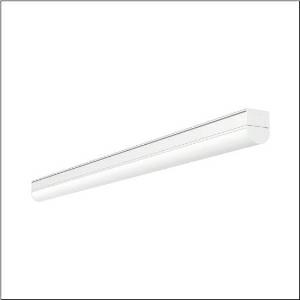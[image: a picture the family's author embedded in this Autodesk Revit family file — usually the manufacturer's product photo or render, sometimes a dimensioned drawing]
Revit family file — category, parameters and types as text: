
# Revit family: ecopack_31_51lj12mnm70a
name_source: partatom
category: Lighting Fixtures
units: mm (PartAtom-declared; Revit-internal decimal feet)

## family parameters
Cut with Voids When Loaded = No
Host = Face
Light Source = No
Part Type = Normal
Room Calculation Point = No
Round Connector Dimension = Use Diameter
Shared = No

## types (1)
- --- (1 x LED, 6780 lm, 50 W, 5000K)
    Apparent Load = 50 VA
    CIE Flux Codes = 39 67 87 89 100
    Color Rendering = 80
    Color Temperature = 5000K
    Default Elevation = 1800 mm
    Description = Ecopack 31, diffuser luminaire, primary optical cover: cover, of PC, frosted, light emission: direct distribution, primary light characteristic: symmetric, installation type: surface-mounted, LED, rated luminous flux: 7.000lm, luminous efficacy: 140lm/W, light colour: 830/840/850, colour temperature: 3000/4000/5000K, control gear: ON/OFF Multilumen, with terminal, 3-pole, mains connection: 220..240V, AC, 50/60Hz, rated input power: 50W, housing, of aluminium, traffic white (RAL 9016), length: 1.450mm, width: 56mm, height: 68mm, end cap, of PC, white, protection rating (complete): IP20, insulation class (complete): insulation class I (protective earthing), certification: CE, impact resistance: IK06, permissible operating ambient temperature: -20..+40°C, packaging unit: 1 piece
    Height = 68 mm
    Lamp = 1 x LED
    Lamp Light Flux = 6780 lm
    Lamp Power = 50 W
    Lamp count = 1
    Length = 1450 mm
    Luminous efficacy = 136 lm/W
    Manufacturer = Siteco
    ModVariant = No
    Model = 51LJ12MNM70A
    Mounting Place = Ceiling
    Mounting Type = Surface mounted
    Number of Poles = 1
    OnlyDefault = Yes
    Power Factor = 1
    Product Name = Ecopack 31
    Product group = diffuser luminaire
    ProductGroupID = 307
    Protection Class = Protection class I
    Protection Degree = IP 20
    RLX_Detail_Level = 1
    RLX_Emergency_Light_Flux = 0 lm
    RLX_Emergency_Type = 0
    RLX_Emergency_Type_DB = No
    RlxData = <blob elided: 39301 chars, md5=3ee0786a>
    Socket = socket
    Standby Power = 0 W
    System Light Flux = 6780 lm
    System Power = 50 W
    Type Comments = individual setting: colour temperature 5000K, luminous flux: 100 % | (ON | ON)
    Type Image = l_1007033.jpg
    URL = http://relux.com
    VarID = @adj_173459
    Voltage = 0 V
    Weight = 0.00 kg
    Width = 56 mm

## geometry (parser evidence)
native form markers: Blend x4, Sweep x14
no freeform markers — native parametric forms only
